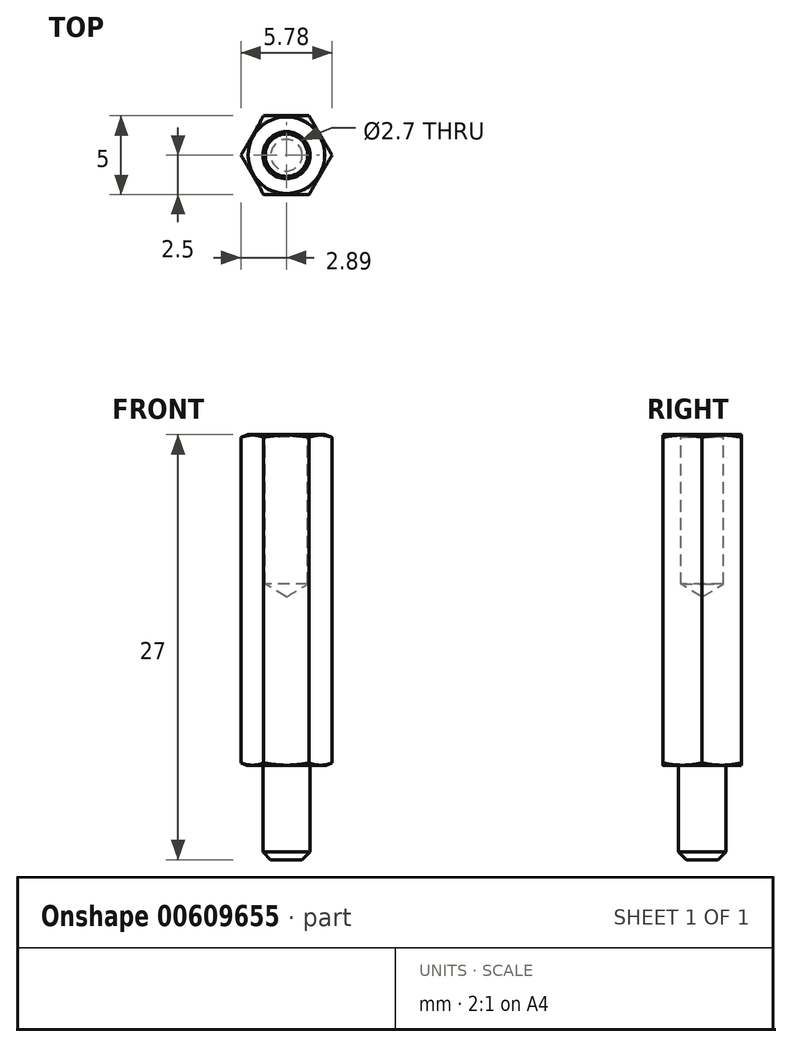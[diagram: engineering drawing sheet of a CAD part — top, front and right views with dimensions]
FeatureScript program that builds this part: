
annotation { "Feature Type Name" : "Feature", "Feature Type Description" : "" }
export const myFeature = defineFeature(function(context is Context, id is Id, definition is map)
    precondition{}
    {
        {
            var Q0;
            Q0=qCreatedBy(makeId("Top.planeOp"),FACE);
            var sketch = newSketch(context, id + "F0", { "sketchPlane" : qUnion([Q0])});
            skCircle(sketch, "E0", {"center": v(0, 0) * mm, "radius": 1.5 * mm});
            skSolve(sketch);
        }
        {
            var Q0;
            Q0 = qSketchRegion(id + "F0", true);
            extrude(context, id + "F1", {"entities" : qUnion([Q0]), "depth" : 6 * mm, "offsetDistance" : 25 * mm});
        }
        {
            var Q0;
            Q0=makeQuery(id+"F1.opExtrude","CAP_FACE",FACE,{"disambiguationData":[OSD([sQuery(id+"F0.wireOp",EDGE,"E0")])],"isStart":false});
            var sketch = newSketch(context, id + "F2", { "sketchPlane" : qUnion([Q0])});
            skCircle(sketch, "E1.cCircle", {"center": v(0, 0) * mm, "radius": 2.5 * mm, "construction": true});
            skLineSegment(sketch, "E1.0", {"start": v(1.44, -2.5) * mm, "end": v(-1.44, -2.5) * mm});
            skLineSegment(sketch, "E1.1", {"start": v(-1.44, -2.5) * mm, "end": v(-2.89, 0) * mm});
            skLineSegment(sketch, "E1.2", {"start": v(-2.89, 0) * mm, "end": v(-1.44, 2.5) * mm});
            skLineSegment(sketch, "E1.3", {"start": v(-1.44, 2.5) * mm, "end": v(1.44, 2.5) * mm});
            skLineSegment(sketch, "E1.4", {"start": v(1.44, 2.5) * mm, "end": v(2.89, 0) * mm});
            skLineSegment(sketch, "E1.5", {"start": v(2.89, 0) * mm, "end": v(1.44, -2.5) * mm});
            skPoint(sketch, "E1.0.midPoint", {"position": v(0, -2.5) * mm});
            skSolve(sketch);
        }
        {
            var Q0;
            Q0 = qSketchRegion(id + "F2", true);
            extrude(context, id + "F3", {"entities" : qUnion([Q0]), "operationType" : NewBodyOperationType.ADD, "depth" : 21 * mm, "offsetDistance" : 25 * mm});
        }
        {
            var Q0;
            Q0=makeQuery(id+"F3.opExtrude","CAP_FACE",FACE,{"disambiguationData":[OSD([sQuery(id+"F2.wireOp",EDGE,"E1.0"),sQuery(id+"F2.wireOp",EDGE,"E1.1"),sQuery(id+"F2.wireOp",EDGE,"E1.2"),sQuery(id+"F2.wireOp",EDGE,"E1.3"),sQuery(id+"F2.wireOp",EDGE,"E1.4"),sQuery(id+"F2.wireOp",EDGE,"E1.5")])],"isStart":false});
            var sketch = newSketch(context, id + "F4", { "sketchPlane" : qUnion([Q0])});
            skPoint(sketch, "E2", {"position": v(0, 0) * mm});
            skSolve(sketch);
        }
        {
            var Q0;
            Q0=sQuery(id+"F4.wireOp",VERTEX,"E2");
            var Q1;
            Q1=makeQuery(id+"F1.opExtrude","SWEPT_BODY",BODY,{"disambiguationData":[OSD([sQuery(id+"F0.wireOp",EDGE,"E0")])]});
            hole(context, id + "F5", {"style" : HoleStyle.C_SINK, "endStyle" : HoleEndStyle.BLIND, "holeDiameter" : 2.7 * mm, "cSinkDiameter" : 3 * mm, "cSinkAngle" : 90 * degree, "majorDiameter" : 3 * mm, "holeDepth" : 9.5 * mm, "tappedDepth" : 8 * mm, "tapClearance" : 3, "locations" : qUnion([Q0]), "scope" : qUnion([Q1])});
        }
        {
            var Q0;
            Q0=qCreatedBy(makeId("Front.planeOp"),FACE);
            var sketch = newSketch(context, id + "F6", { "sketchPlane" : qUnion([Q0])});
            skLineSegment(sketch, "E3", {"start": v(-3.7, 6) * mm, "end": v(-2.5, 6) * mm});
            skLineSegment(sketch, "E4", {"start": v(-2.5, 6) * mm, "end": v(-3.7, 6.46) * mm});
            skLineSegment(sketch, "E5", {"start": v(-3.7, 6.46) * mm, "end": v(-3.7, 6) * mm});
            skLineSegment(sketch, "E6.MirrorCS", {"start": v(-2.43, 27) * mm, "end": v(-3.62, 26.54) * mm});
            skLineSegment(sketch, "E7.MirrorCS", {"start": v(-3.62, 27) * mm, "end": v(-2.43, 27) * mm});
            skLineSegment(sketch, "E8.MirrorCS", {"start": v(-3.62, 26.54) * mm, "end": v(-3.62, 27) * mm});
            skLineSegment(sketch, "E9", {"start": v(0, 0) * mm, "end": v(0, 28.52) * mm, "construction": true});
            skSolve(sketch);
        }
        {
            var Q0;
            Q0 = qSketchRegion(id + "F6", true);
            var Q1;
            Q1=sQuery(id+"F6.wireOp",EDGE,"E9");
            revolve(context, id + "F7", {"operationType" : NewBodyOperationType.REMOVE, "entities" : qUnion([Q0]), "axis" : qUnion([Q1]), "revolveType" : RevolveType.FULL, "oppositeDirection" : true});
        }
        {
            var Q0;
            Q0=makeQuery(id+"F1.opExtrude","CAP_EDGE",EDGE,{"disambiguationData":[OSD([sQuery(id+"F0.wireOp",EDGE,"E0")])],"isStart":true});
            chamfer(context, id + "F8", {"entities" : qUnion([Q0]), "width" : 0.5 * mm, "tangentPropagation" : true});
        }
    });
